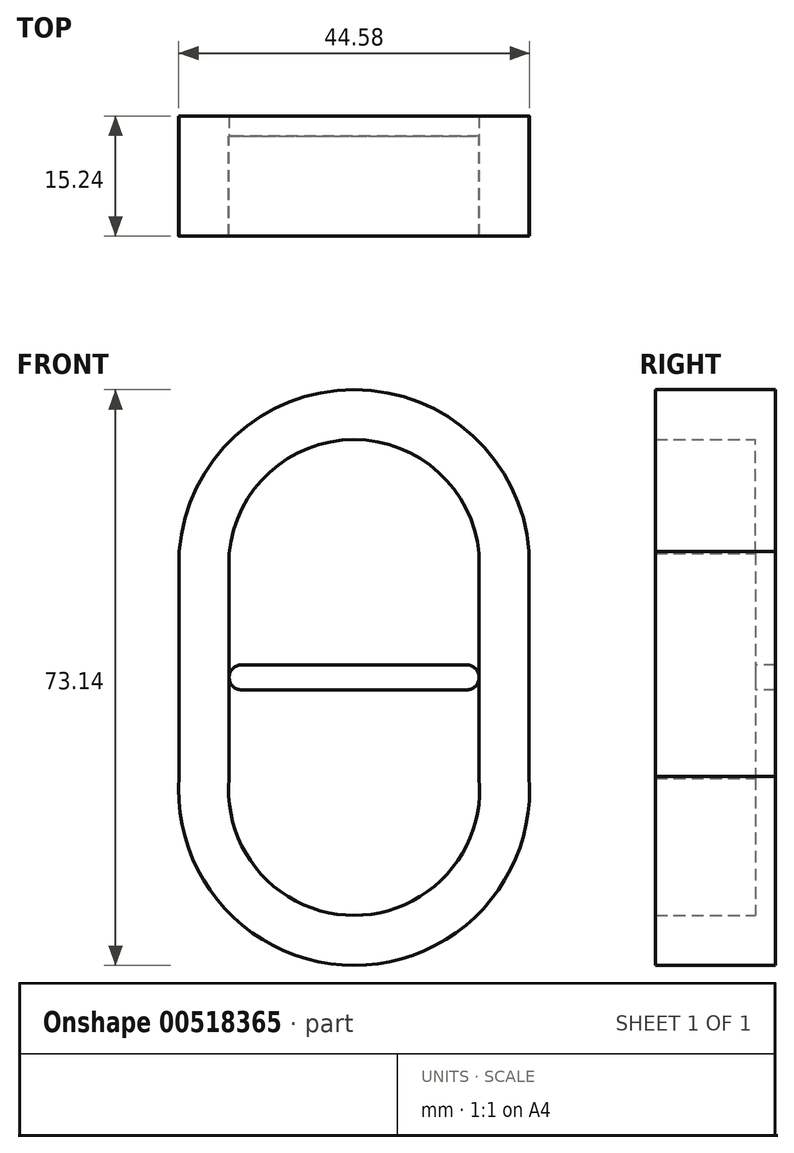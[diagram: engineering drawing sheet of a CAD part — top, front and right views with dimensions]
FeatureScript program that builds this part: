
annotation { "Feature Type Name" : "Feature", "Feature Type Description" : "" }
export const myFeature = defineFeature(function(context is Context, id is Id, definition is map)
    precondition{}
    {
        {
            var Q0;
            Q0=qCreatedBy(makeId("Front.planeOp"),FACE);
            var sketch = newSketch(context, id + "F0", { "sketchPlane" : qUnion([Q0])});
            skCircle(sketch, "E0", {"center": v(0, 0) * mm, "radius": 1.59 * mm});
            skLineSegment(sketch, "E1", {"start": v(0, 0) * mm, "end": v(0, 10.57) * mm, "construction": true});
            skLineSegment(sketch, "E2", {"start": v(-13.12, 0) * mm, "end": v(16.97, 0) * mm, "construction": true});
            skLineSegment(sketch, "E3", {"start": v(-22.23, 16.03) * mm, "end": v(-22.22, -12.55) * mm});
            skLineSegment(sketch, "E4.MirrorCS", {"start": v(22.23, 16.03) * mm, "end": v(22.22, -12.55) * mm});
            skArc(sketch, "E5.trimOffspring", {"start": v(22.23, -12.55) * mm, "mid": v(0, -36.58) * mm, "end": v(-22.23, -12.55) * mm});
            skArc(sketch, "E6.trimOffspring", {"start": v(22.23, 16.03) * mm, "mid": v(0, 36.56) * mm, "end": v(-22.23, 16.03) * mm});
            skPoint(sketch, "E7.center.orphan", {"position": v(0, 14.29) * mm});
            skSolve(sketch);
        }
        {
            var Q0;
            Q0 = qSketchRegion(id + "F0", true);
            extrude(context, id + "F1", {"entities" : qUnion([Q0]), "depth" : 2.54 * mm, "offsetDistance" : 25.4 * mm});
        }
        {
            var Q0;
            Q0=makeQuery(id+"F1.opExtrude","CAP_FACE",FACE,{"disambiguationData":[OSD([sQuery(id+"F0.wireOp",EDGE,"E0"),sQuery(id+"F0.wireOp",EDGE,"E3"),sQuery(id+"F0.wireOp",EDGE,"E4.MirrorCS"),sQuery(id+"F0.wireOp",EDGE,"E5.trimOffspring"),sQuery(id+"F0.wireOp",EDGE,"E6.trimOffspring")])],"isStart":false});
            var sketch = newSketch(context, id + "F2", { "sketchPlane" : qUnion([Q0])});
            skLineSegment(sketch, "E8", {"start": v(0, 1.59) * mm, "end": v(14.29, 1.59) * mm});
            skLineSegment(sketch, "E9", {"start": v(0, 0) * mm, "end": v(12.72, 0) * mm, "construction": true});
            skLineSegment(sketch, "E10", {"start": v(0, 0) * mm, "end": v(0, 12.6) * mm, "construction": true});
            skArc(sketch, "E11", {"start": v(14.29, -1.59) * mm, "mid": v(15.88, 0) * mm, "end": v(14.29, 1.59) * mm});
            skLineSegment(sketch, "E12.MirrorCS", {"start": v(0, -1.59) * mm, "end": v(14.29, -1.59) * mm});
            skLineSegment(sketch, "E13.MirrorCS", {"start": v(0, 1.59) * mm, "end": v(-14.29, 1.59) * mm});
            skLineSegment(sketch, "E14.MirrorCS", {"start": v(0, -1.59) * mm, "end": v(-14.29, -1.59) * mm});
            skArc(sketch, "E15.MirrorCS", {"start": v(-14.29, -1.59) * mm, "mid": v(-15.88, 0) * mm, "end": v(-14.29, 1.59) * mm});
            skSolve(sketch);
        }
        {
            var Q0;
            Q0 = qSketchRegion(id + "F2", true);
            extrude(context, id + "F3", {"entities" : qUnion([Q0]), "operationType" : NewBodyOperationType.REMOVE, "endBound" : BoundingType.THROUGH_ALL, "oppositeDirection" : true, "depth" : 25.4 * mm, "offsetDistance" : 25.4 * mm});
        }
        {
            var Q0;
            Q0=makeQuery(id+"F1.opExtrude","CAP_FACE",FACE,{"disambiguationData":[OSD([sQuery(id+"F0.wireOp",EDGE,"E0"),sQuery(id+"F0.wireOp",EDGE,"E3"),sQuery(id+"F0.wireOp",EDGE,"E4.MirrorCS"),sQuery(id+"F0.wireOp",EDGE,"E5.trimOffspring"),sQuery(id+"F0.wireOp",EDGE,"E6.trimOffspring")])],"isStart":false});
            var sketch = newSketch(context, id + "F4", { "sketchPlane" : qUnion([Q0])});
            skArc(sketch, "E16.0", {"start": v(15.88, 15.75) * mm, "mid": v(0, 30.21) * mm, "end": v(-15.88, 15.75) * mm});
            skLineSegment(sketch, "E16.1", {"start": v(15.88, 15.75) * mm, "end": v(15.88, -12.82) * mm});
            skArc(sketch, "E16.2", {"start": v(15.88, -12.82) * mm, "mid": v(0, -30.23) * mm, "end": v(-15.88, -12.82) * mm});
            skLineSegment(sketch, "E16.3", {"start": v(-15.88, 15.75) * mm, "end": v(-15.88, -12.82) * mm});
            skArc(sketch, "E17.0", {"start": v(22.23, 16.03) * mm, "mid": v(0, 36.56) * mm, "end": v(-22.23, 16.03) * mm});
            skLineSegment(sketch, "E17.1", {"start": v(22.23, 16.03) * mm, "end": v(22.23, -12.55) * mm});
            skArc(sketch, "E17.2", {"start": v(22.23, -12.55) * mm, "mid": v(0, -36.58) * mm, "end": v(-22.23, -12.55) * mm});
            skLineSegment(sketch, "E17.3", {"start": v(-22.23, 16.03) * mm, "end": v(-22.23, -12.55) * mm});
            skSolve(sketch);
        }
        {
            var Q0;
            Q0 = qSketchRegion(id + "F4", true);
            extrude(context, id + "F5", {"entities" : qUnion([Q0]), "operationType" : NewBodyOperationType.ADD, "depth" : 12.7 * mm, "offsetDistance" : 25.4 * mm});
        }
    });
